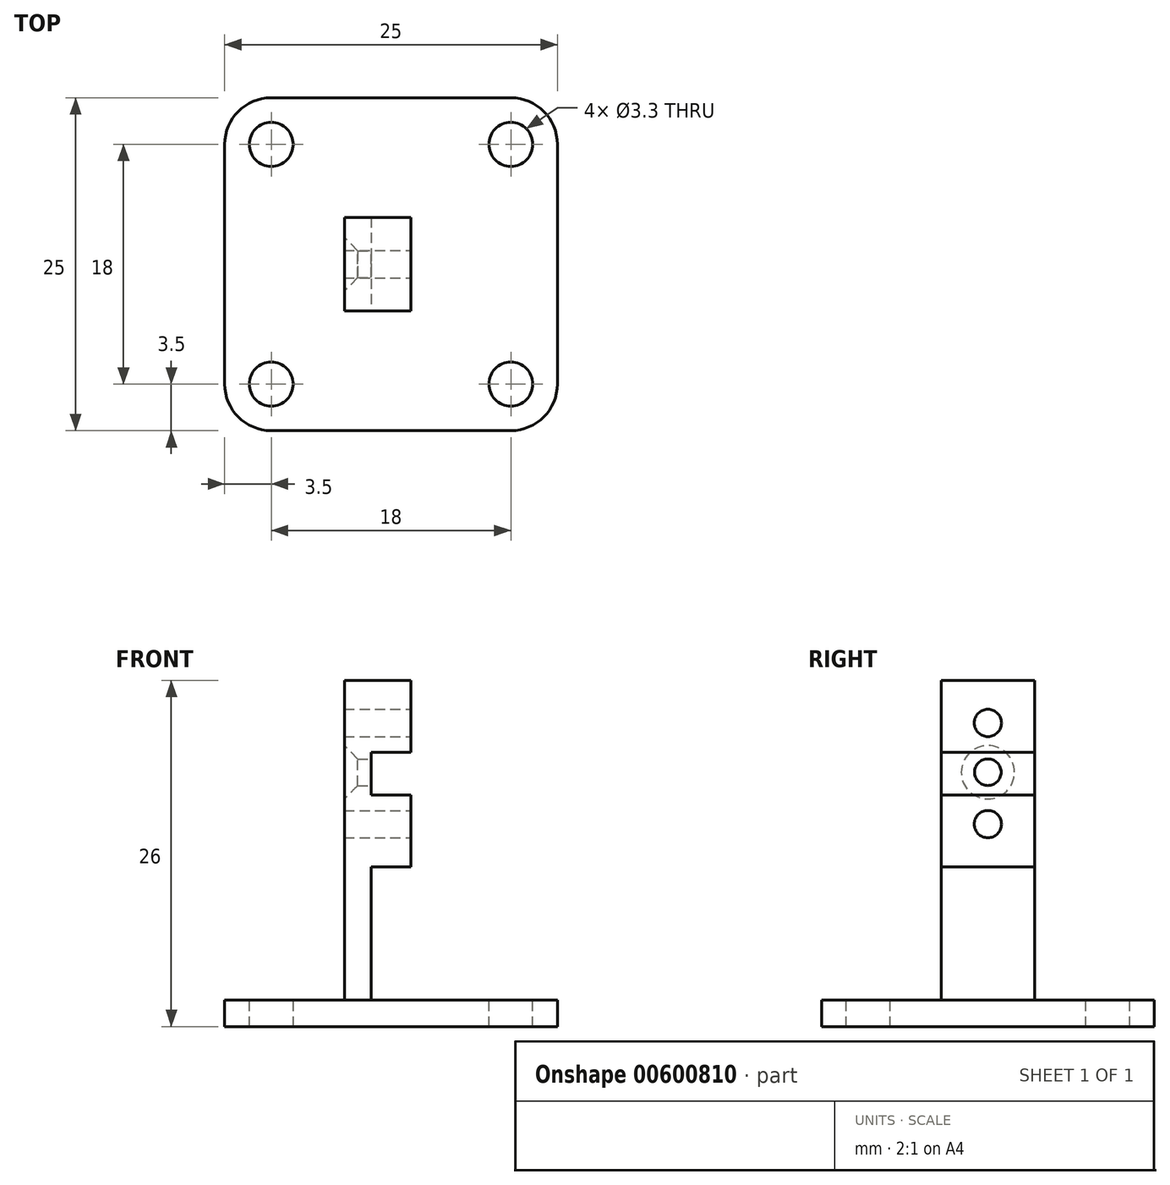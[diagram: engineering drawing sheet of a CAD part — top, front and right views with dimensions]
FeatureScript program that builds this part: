
annotation { "Feature Type Name" : "Feature", "Feature Type Description" : "" }
export const myFeature = defineFeature(function(context is Context, id is Id, definition is map)
    precondition{}
    {
        {
            var Q0;
            Q0=qCreatedBy(makeId("Top.planeOp"),FACE);
            var sketch = newSketch(context, id + "F0", { "sketchPlane" : qUnion([Q0])});
            skLineSegment(sketch, "E0.bottom", {"start": v(0, 0) * mm, "end": v(25, 0) * mm});
            skLineSegment(sketch, "E0.top", {"start": v(0, 25) * mm, "end": v(25, 25) * mm});
            skLineSegment(sketch, "E0.left", {"start": v(0, 0) * mm, "end": v(0, 25) * mm});
            skLineSegment(sketch, "E0.right", {"start": v(25, 0) * mm, "end": v(25, 25) * mm});
            skSolve(sketch);
        }
        {
            var Q0;
            Q0=makeQuery(id+"F0.imprint","IMPRINT",FACE,{"disambiguationData":[TD([[makeQuery(id+"F0.imprint","IMPRINT",EDGE,{"derivedFrom":sQuery(id+"F0.wireOp",EDGE,"E0.bottom")}),1.0]])]});
            extrude(context, id + "F1", {"entities" : qUnion([Q0]), "depth" : 2 * mm, "offsetDistance" : 25 * mm});
        }
        {
            var Q0;
            Q0=makeQuery(id+"F1.opExtrude","CAP_FACE",FACE,{"disambiguationData":[OSD([sQuery(id+"F0.wireOp",EDGE,"E0.bottom"),sQuery(id+"F0.wireOp",EDGE,"E0.top"),sQuery(id+"F0.wireOp",EDGE,"E0.left"),sQuery(id+"F0.wireOp",EDGE,"E0.right")])],"isStart":false});
            var sketch = newSketch(context, id + "F2", { "sketchPlane" : qUnion([Q0])});
            skCircle(sketch, "E1", {"center": v(3.5, 21.5) * mm, "radius": 1.65 * mm});
            skSolve(sketch);
        }
        {
            var Q0;
            Q0=makeQuery(id+"F2.imprint","IMPRINT",FACE,{"disambiguationData":[TD([[makeQuery(id+"F2.imprint","IMPRINT",EDGE,{"derivedFrom":sQuery(id+"F2.wireOp",EDGE,"E1")}),-1.0]])]});
            var sketch = newSketch(context, id + "F3", { "sketchPlane" : qUnion([Q0])});
            skCircle(sketch, "E2", {"center": v(21.5, 21.5) * mm, "radius": 1.65 * mm});
            skSolve(sketch);
        }
        {
            var Q0;
            Q0=makeQuery(id+"F2.imprint","IMPRINT",FACE,{"disambiguationData":[TD([[makeQuery(id+"F2.imprint","IMPRINT",EDGE,{"derivedFrom":sQuery(id+"F2.wireOp",EDGE,"E1")}),-1.0]])]});
            var sketch = newSketch(context, id + "F4", { "sketchPlane" : qUnion([Q0])});
            skCircle(sketch, "E3", {"center": v(3.5, 3.5) * mm, "radius": 1.65 * mm});
            skSolve(sketch);
        }
        {
            var Q0;
            Q0=makeQuery(id+"F2.imprint","IMPRINT",FACE,{"disambiguationData":[TD([[makeQuery(id+"F2.imprint","IMPRINT",EDGE,{"derivedFrom":sQuery(id+"F2.wireOp",EDGE,"E1")}),-1.0]])]});
            var sketch = newSketch(context, id + "F5", { "sketchPlane" : qUnion([Q0])});
            skCircle(sketch, "E4", {"center": v(21.5, 3.5) * mm, "radius": 1.65 * mm});
            skSolve(sketch);
        }
        {
            var Q0;
            Q0=makeQuery(id+"F2.imprint","IMPRINT",FACE,{"disambiguationData":[TD([[makeQuery(id+"F2.imprint","IMPRINT",EDGE,{"derivedFrom":sQuery(id+"F2.wireOp",EDGE,"E1")}),1.0]])]});
            extrude(context, id + "F6", {"entities" : qUnion([Q0]), "operationType" : NewBodyOperationType.REMOVE, "oppositeDirection" : true, "depth" : 3 * mm, "offsetDistance" : 25 * mm});
        }
        {
            var Q0;
            Q0=makeQuery(id+"F3.imprint","IMPRINT",FACE,{"disambiguationData":[TD([[makeQuery(id+"F3.imprint","IMPRINT",EDGE,{"derivedFrom":sQuery(id+"F3.wireOp",EDGE,"E2")}),1.0]])]});
            extrude(context, id + "F7", {"entities" : qUnion([Q0]), "operationType" : NewBodyOperationType.REMOVE, "oppositeDirection" : true, "depth" : 3 * mm, "offsetDistance" : 25 * mm});
        }
        {
            var Q0;
            Q0=makeQuery(id+"F4.imprint","IMPRINT",FACE,{"disambiguationData":[TD([[makeQuery(id+"F4.imprint","IMPRINT",EDGE,{"derivedFrom":sQuery(id+"F4.wireOp",EDGE,"E3")}),1.0]])]});
            extrude(context, id + "F8", {"entities" : qUnion([Q0]), "operationType" : NewBodyOperationType.REMOVE, "oppositeDirection" : true, "depth" : 3 * mm, "offsetDistance" : 25 * mm});
        }
        {
            var Q0;
            Q0=makeQuery(id+"F5.imprint","IMPRINT",FACE,{"disambiguationData":[TD([[makeQuery(id+"F5.imprint","IMPRINT",EDGE,{"derivedFrom":sQuery(id+"F5.wireOp",EDGE,"E4")}),1.0]])]});
            extrude(context, id + "F9", {"entities" : qUnion([Q0]), "operationType" : NewBodyOperationType.REMOVE, "oppositeDirection" : true, "depth" : 3 * mm, "offsetDistance" : 25 * mm});
        }
        {
            var Q0;
            Q0=makeQuery(id+"F1.opExtrude","SWEPT_EDGE",EDGE,{"disambiguationData":[OSD([sQuery(id+"F0.wireOp",EDGE,"E0.bottom"),sQuery(id+"F0.wireOp",EDGE,"E0.left")])]});
            var Q1;
            Q1=makeQuery(id+"F1.opExtrude","SWEPT_EDGE",EDGE,{"disambiguationData":[OSD([sQuery(id+"F0.wireOp",EDGE,"E0.top"),sQuery(id+"F0.wireOp",EDGE,"E0.left")])]});
            var Q2;
            Q2=makeQuery(id+"F1.opExtrude","SWEPT_EDGE",EDGE,{"disambiguationData":[OSD([sQuery(id+"F0.wireOp",EDGE,"E0.top"),sQuery(id+"F0.wireOp",EDGE,"E0.right")])]});
            var Q3;
            Q3=makeQuery(id+"F1.opExtrude","SWEPT_EDGE",EDGE,{"disambiguationData":[OSD([sQuery(id+"F0.wireOp",EDGE,"E0.bottom"),sQuery(id+"F0.wireOp",EDGE,"E0.right")])]});
            fillet(context, id + "F10", {"entities" : qUnion([Q0, Q1, Q2, Q3]), "radius" : 3.5 * mm, "tangentPropagation" : true, "allowEdgeOverflow" : false});
        }
        {
            var Q0;
            Q0=makeQuery(id+"F1.opExtrude","CAP_FACE",FACE,{"disambiguationData":[OSD([sQuery(id+"F0.wireOp",EDGE,"E0.bottom"),sQuery(id+"F0.wireOp",EDGE,"E0.top"),sQuery(id+"F0.wireOp",EDGE,"E0.left"),sQuery(id+"F0.wireOp",EDGE,"E0.right")])],"isStart":false});
            var sketch = newSketch(context, id + "F11", { "sketchPlane" : qUnion([Q0])});
            skLineSegment(sketch, "E5.bottom", {"start": v(9, 16) * mm, "end": v(11, 16) * mm});
            skLineSegment(sketch, "E5.top", {"start": v(9, 9) * mm, "end": v(11, 9) * mm});
            skLineSegment(sketch, "E5.left", {"start": v(9, 16) * mm, "end": v(9, 9) * mm});
            skLineSegment(sketch, "E5.right", {"start": v(11, 16) * mm, "end": v(11, 9) * mm});
            skSolve(sketch);
        }
        {
            var Q0;
            Q0=makeQuery(id+"F11.imprint","IMPRINT",FACE,{"disambiguationData":[TD([[makeQuery(id+"F11.imprint","IMPRINT",EDGE,{"derivedFrom":sQuery(id+"F11.wireOp",EDGE,"E5.bottom")}),-1.0]])]});
            extrude(context, id + "F12", {"entities" : qUnion([Q0]), "operationType" : NewBodyOperationType.ADD, "depth" : 23 * mm, "offsetDistance" : 25 * mm});
        }
        {
            var Q0;
            Q0=makeQuery(id+"F12.opExtrude","SWEPT_FACE",FACE,{"disambiguationData":[OSD([sQuery(id+"F11.wireOp",EDGE,"E5.right")])]});
            var sketch = newSketch(context, id + "F13", { "sketchPlane" : qUnion([Q0])});
            skCircle(sketch, "E6", {"center": v(12.5, 19.1) * mm, "radius": 1 * mm});
            skSolve(sketch);
        }
        {
            var Q0;
            Q0=makeQuery(id+"F13.imprint","IMPRINT",FACE,{"disambiguationData":[TD([[makeQuery(id+"F13.imprint","IMPRINT",EDGE,{"derivedFrom":sQuery(id+"F13.wireOp",EDGE,"E6")}),-1.0]])]});
            var sketch = newSketch(context, id + "F14", { "sketchPlane" : qUnion([Q0])});
            skLineSegment(sketch, "E7.bottom", {"start": v(16, 25) * mm, "end": v(9, 25) * mm});
            skLineSegment(sketch, "E7.top", {"start": v(16, 13) * mm, "end": v(9, 13) * mm});
            skLineSegment(sketch, "E7.left", {"start": v(16, 25) * mm, "end": v(16, 13) * mm});
            skLineSegment(sketch, "E7.right", {"start": v(9, 25) * mm, "end": v(9, 13) * mm});
            skSolve(sketch);
        }
        {
            var Q0;
            Q0 = qSketchRegion(id + "F14", true);
            extrude(context, id + "F15", {"entities" : qUnion([Q0]), "operationType" : NewBodyOperationType.ADD, "depth" : 3 * mm, "offsetDistance" : 25 * mm});
        }
        {
            var Q0;
            Q0=makeQuery(id+"F15.opExtrude","CAP_FACE",FACE,{"disambiguationData":[OSD([sQuery(id+"F14.wireOp",EDGE,"E7.bottom"),sQuery(id+"F14.wireOp",EDGE,"E7.top"),sQuery(id+"F14.wireOp",EDGE,"E7.left"),sQuery(id+"F14.wireOp",EDGE,"E7.right")])],"isStart":false});
            var sketch = newSketch(context, id + "F16", { "sketchPlane" : qUnion([Q0])});
            skLineSegment(sketch, "E8.bottom", {"start": v(9, 20.6) * mm, "end": v(16, 20.6) * mm});
            skLineSegment(sketch, "E8.top", {"start": v(9, 17.4) * mm, "end": v(16, 17.4) * mm});
            skLineSegment(sketch, "E8.left", {"start": v(9, 20.6) * mm, "end": v(9, 17.4) * mm});
            skLineSegment(sketch, "E8.right", {"start": v(16, 20.6) * mm, "end": v(16, 17.4) * mm});
            skSolve(sketch);
        }
        {
            var Q0;
            Q0=makeQuery(id+"F16.imprint","IMPRINT",FACE,{"disambiguationData":[TD([[makeQuery(id+"F16.imprint","IMPRINT",EDGE,{"derivedFrom":sQuery(id+"F16.wireOp",EDGE,"E8.bottom")}),-1.0]])]});
            extrude(context, id + "F17", {"entities" : qUnion([Q0]), "operationType" : NewBodyOperationType.REMOVE, "oppositeDirection" : true, "depth" : 3 * mm, "offsetDistance" : 25 * mm});
        }
        {
            var Q0;
            {var subQ0=sQuery(id+"F14.wireOp",EDGE,"E7.bottom");var subQ3=sQuery(id+"F14.wireOp",EDGE,"E7.left");var subQ4=sQuery(id+"F14.wireOp",EDGE,"E7.right");Q0=makeQuery(id+"F17.boolean.opBoolean","SPLIT",FACE,{"disambiguationData":[TD([makeQuery(id+"F15.opExtrude","SWEPT_FACE",FACE,{"disambiguationData":[OSD([subQ0])]})])],"derivedFrom":makeQuery(id+"F15.opExtrude","CAP_FACE",FACE,{"disambiguationData":[OSD([subQ0,sQuery(id+"F14.wireOp",EDGE,"E7.top"),subQ3,subQ4])],"isStart":false})});}
            var sketch = newSketch(context, id + "F18", { "sketchPlane" : qUnion([Q0])});
            skCircle(sketch, "E9", {"center": v(12.5, 22.8) * mm, "radius": 1.02 * mm});
            skSolve(sketch);
        }
        {
            var Q0;
            {var subQ0=sQuery(id+"F14.wireOp",EDGE,"E7.top");var subQ1=sQuery(id+"F14.wireOp",EDGE,"E7.left");var subQ2=sQuery(id+"F14.wireOp",EDGE,"E7.right");Q0=makeQuery(id+"F17.boolean.opBoolean","SPLIT",FACE,{"disambiguationData":[TD([makeQuery(id+"F15.opExtrude","SWEPT_FACE",FACE,{"disambiguationData":[OSD([subQ0])]})])],"derivedFrom":makeQuery(id+"F15.opExtrude","CAP_FACE",FACE,{"disambiguationData":[OSD([sQuery(id+"F14.wireOp",EDGE,"E7.bottom"),subQ0,subQ1,subQ2])],"isStart":false})});}
            var sketch = newSketch(context, id + "F19", { "sketchPlane" : qUnion([Q0])});
            skCircle(sketch, "E10", {"center": v(12.5, 15.2) * mm, "radius": 1.02 * mm});
            skSolve(sketch);
        }
        {
            var Q0;
            Q0=makeQuery(id+"F19.imprint","IMPRINT",FACE,{"disambiguationData":[TD([[makeQuery(id+"F19.imprint","IMPRINT",EDGE,{"derivedFrom":sQuery(id+"F19.wireOp",EDGE,"E10")}),1.0]])]});
            extrude(context, id + "F20", {"entities" : qUnion([Q0]), "operationType" : NewBodyOperationType.REMOVE, "oppositeDirection" : true, "depth" : 6 * mm, "offsetDistance" : 25 * mm});
        }
        {
            var Q0;
            Q0=makeQuery(id+"F18.imprint","IMPRINT",FACE,{"disambiguationData":[TD([[makeQuery(id+"F18.imprint","IMPRINT",EDGE,{"derivedFrom":sQuery(id+"F18.wireOp",EDGE,"E9")}),1.0]])]});
            extrude(context, id + "F21", {"entities" : qUnion([Q0]), "operationType" : NewBodyOperationType.REMOVE, "oppositeDirection" : true, "depth" : 6 * mm, "offsetDistance" : 25 * mm});
        }
        {
            var Q0;
            Q0=makeQuery(id+"F13.imprint","IMPRINT",FACE,{"disambiguationData":[TD([[makeQuery(id+"F13.imprint","IMPRINT",EDGE,{"derivedFrom":sQuery(id+"F13.wireOp",EDGE,"E6")}),1.0]])]});
            extrude(context, id + "F22", {"entities" : qUnion([Q0]), "operationType" : NewBodyOperationType.REMOVE, "oppositeDirection" : true, "depth" : 3 * mm, "offsetDistance" : 25 * mm});
        }
        {
            var Q0;
            Q0=makeQuery(id+"F22.boolean.opBoolean","INTERSECT",EDGE,{"derivedFrom":[makeQuery(id+"F12.opExtrude","SWEPT_FACE",FACE,{"disambiguationData":[OSD([sQuery(id+"F11.wireOp",EDGE,"E5.left")])]}),makeQuery(id+"F22.opExtrude","SWEPT_FACE",FACE,{"disambiguationData":[OSD([sQuery(id+"F13.wireOp",EDGE,"E6")])]})]});
            chamfer(context, id + "F23", {"entities" : qUnion([Q0]), "width" : 1 * mm, "tangentPropagation" : true});
        }
        {
            var Q0;
            Q0=makeQuery(id+"F15.boolean.opBoolean","MERGE",FACE,{"derivedFrom":[makeQuery(id+"F12.opExtrude","CAP_FACE",FACE,{"disambiguationData":[OSD([sQuery(id+"F11.wireOp",EDGE,"E5.bottom"),sQuery(id+"F11.wireOp",EDGE,"E5.top"),sQuery(id+"F11.wireOp",EDGE,"E5.left"),sQuery(id+"F11.wireOp",EDGE,"E5.right")])],"isStart":false}),makeQuery(id+"F15.opExtrude","SWEPT_FACE",FACE,{"disambiguationData":[OSD([sQuery(id+"F14.wireOp",EDGE,"E7.bottom")])]})]});
            extrude(context, id + "F24", {"entities" : qUnion([Q0]), "operationType" : NewBodyOperationType.ADD, "depth" : 1 * mm, "offsetDistance" : 25 * mm});
        }
        {
            var Q0;
            Q0=makeQuery(id+"F15.opExtrude","SWEPT_FACE",FACE,{"disambiguationData":[OSD([sQuery(id+"F14.wireOp",EDGE,"E7.top")])]});
            extrude(context, id + "F25", {"entities" : qUnion([Q0]), "operationType" : NewBodyOperationType.ADD, "depth" : 1 * mm, "offsetDistance" : 25 * mm});
        }
    });
